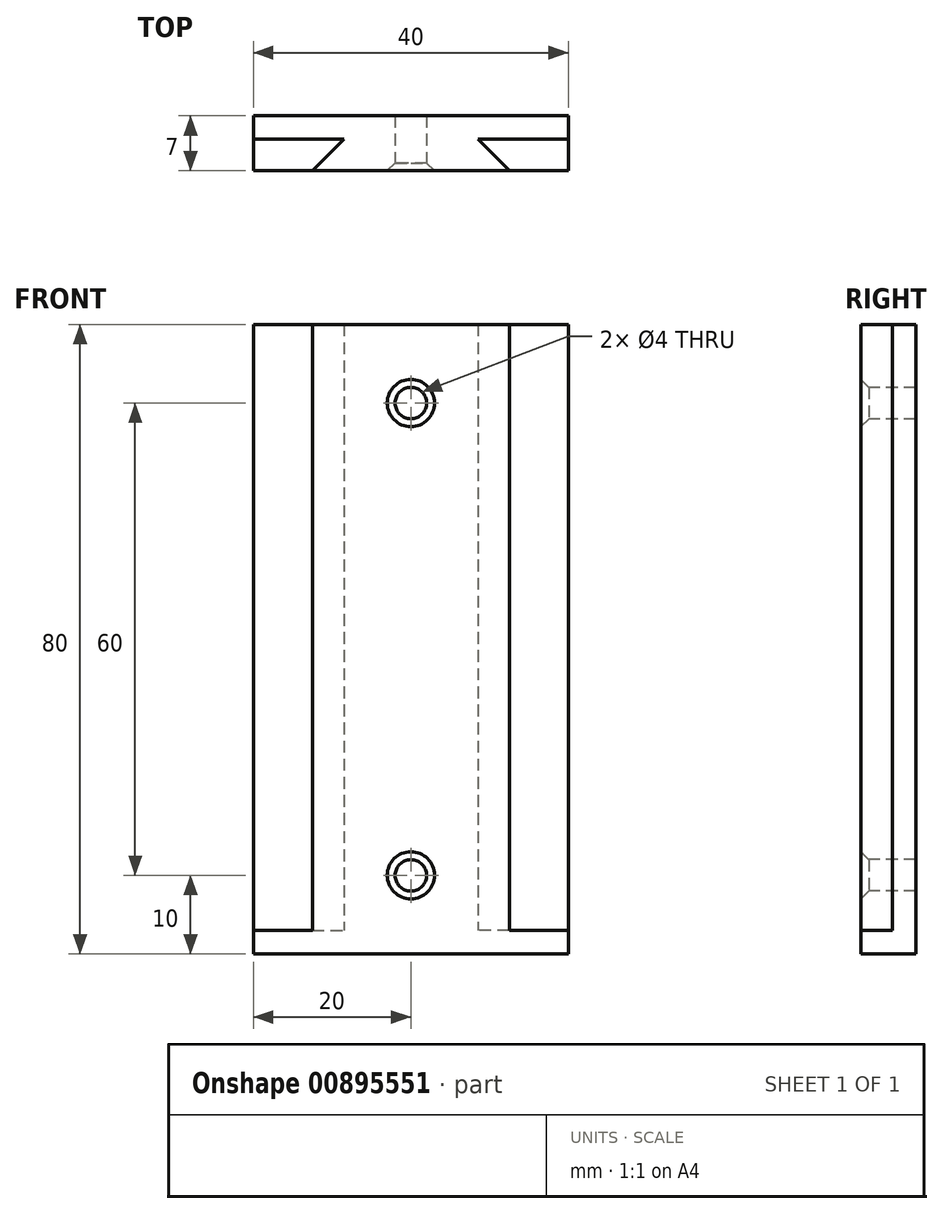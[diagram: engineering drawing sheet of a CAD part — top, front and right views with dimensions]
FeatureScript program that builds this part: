
annotation { "Feature Type Name" : "Feature", "Feature Type Description" : "" }
export const myFeature = defineFeature(function(context is Context, id is Id, definition is map)
    precondition{}
    {
        {
            var Q0;
            Q0=qCreatedBy(makeId("Top.planeOp"),FACE);
            var sketch = newSketch(context, id + "F0", { "sketchPlane" : qUnion([Q0])});
            skLineSegment(sketch, "E0.bottom", {"start": v(-20, 1.5) * mm, "end": v(20, 1.5) * mm});
            skLineSegment(sketch, "E0.top", {"start": v(-20, -1.5) * mm, "end": v(20, -1.5) * mm});
            skLineSegment(sketch, "E0.left", {"start": v(-20, 1.5) * mm, "end": v(-20, -1.5) * mm});
            skLineSegment(sketch, "E0.right", {"start": v(20, 1.5) * mm, "end": v(20, -1.5) * mm});
            skLineSegment(sketch, "E1", {"start": v(-8.5, -1.5) * mm, "end": v(-12.5, -5.5) * mm});
            skLineSegment(sketch, "E2", {"start": v(-12.5, -5.5) * mm, "end": v(12.5, -5.5) * mm});
            skLineSegment(sketch, "E3", {"start": v(12.5, -5.5) * mm, "end": v(8.5, -1.5) * mm});
            skSolve(sketch);
        }
        {
            var Q0;
            Q0 = qSketchRegion(id + "F0", true);
            extrude(context, id + "F1", {"entities" : qUnion([Q0]), "depth" : 80 * mm, "offsetDistance" : 25 * mm});
        }
        {
            var Q0;
            {var subQ0=sQuery(id+"F0.wireOp",EDGE,"E0.top");Q0=makeQuery(id+"F1.opExtrude","SWEPT_FACE",FACE,{"disambiguationData":[OSD([subQ0]),TDD([makeQuery(id+"F0.imprint","IMPRINT",EDGE,{"disambiguationData":[TD([[makeQuery(id+"F0.imprint","INTERSECT",VERTEX,{"derivedFrom":[subQ0,sQuery(id+"F0.wireOp",EDGE,"E0.left")]}),-1.0]])],"derivedFrom":subQ0})])]});}
            var sketch = newSketch(context, id + "F2", { "sketchPlane" : qUnion([Q0])});
            skCircle(sketch, "E4", {"center": v(0, 70) * mm, "radius": 2 * mm});
            skCircle(sketch, "E5", {"center": v(0, 10) * mm, "radius": 2 * mm});
            skSolve(sketch);
        }
        {
            var Q0;
            Q0 = qSketchRegion(id + "F2", true);
            extrude(context, id + "F3", {"entities" : qUnion([Q0]), "operationType" : NewBodyOperationType.REMOVE, "endBound" : BoundingType.SYMMETRIC, "oppositeDirection" : true, "depth" : 25 * mm, "offsetDistance" : 25 * mm});
        }
        {
            var Q0;
            Q0=makeQuery(id+"F3.boolean.opBoolean","INTERSECT",EDGE,{"derivedFrom":[makeQuery(id+"F1.opExtrude","SWEPT_FACE",FACE,{"disambiguationData":[OSD([sQuery(id+"F0.wireOp",EDGE,"E2")])]}),makeQuery(id+"F3.opExtrude","SWEPT_FACE",FACE,{"disambiguationData":[OSD([sQuery(id+"F2.wireOp",EDGE,"E4")])]})]});
            var Q1;
            Q1=makeQuery(id+"F3.boolean.opBoolean","INTERSECT",EDGE,{"derivedFrom":[makeQuery(id+"F1.opExtrude","SWEPT_FACE",FACE,{"disambiguationData":[OSD([sQuery(id+"F0.wireOp",EDGE,"E2")])]}),makeQuery(id+"F3.opExtrude","SWEPT_FACE",FACE,{"disambiguationData":[OSD([sQuery(id+"F2.wireOp",EDGE,"E5")])]})]});
            chamfer(context, id + "F4", {"entities" : qUnion([Q0, Q1]), "width" : 1 * mm, "tangentPropagation" : true});
        }
        {
            var Q0;
            Q0=qCreatedBy(makeId("Top.planeOp"),FACE);
            var sketch = newSketch(context, id + "F5", { "sketchPlane" : qUnion([Q0])});
            skLineSegment(sketch, "E6.bottom", {"start": v(-20, -1.5) * mm, "end": v(20, -1.5) * mm});
            skLineSegment(sketch, "E6.top", {"start": v(-20, -5.5) * mm, "end": v(20, -5.5) * mm});
            skLineSegment(sketch, "E6.left", {"start": v(-20, -1.5) * mm, "end": v(-20, -5.5) * mm});
            skLineSegment(sketch, "E6.right", {"start": v(20, -1.5) * mm, "end": v(20, -5.5) * mm});
            skSolve(sketch);
        }
        {
            var Q0;
            Q0 = qSketchRegion(id + "F5", true);
            extrude(context, id + "F6", {"entities" : qUnion([Q0]), "operationType" : NewBodyOperationType.ADD, "depth" : 3 * mm, "offsetDistance" : 25 * mm});
        }
    });
